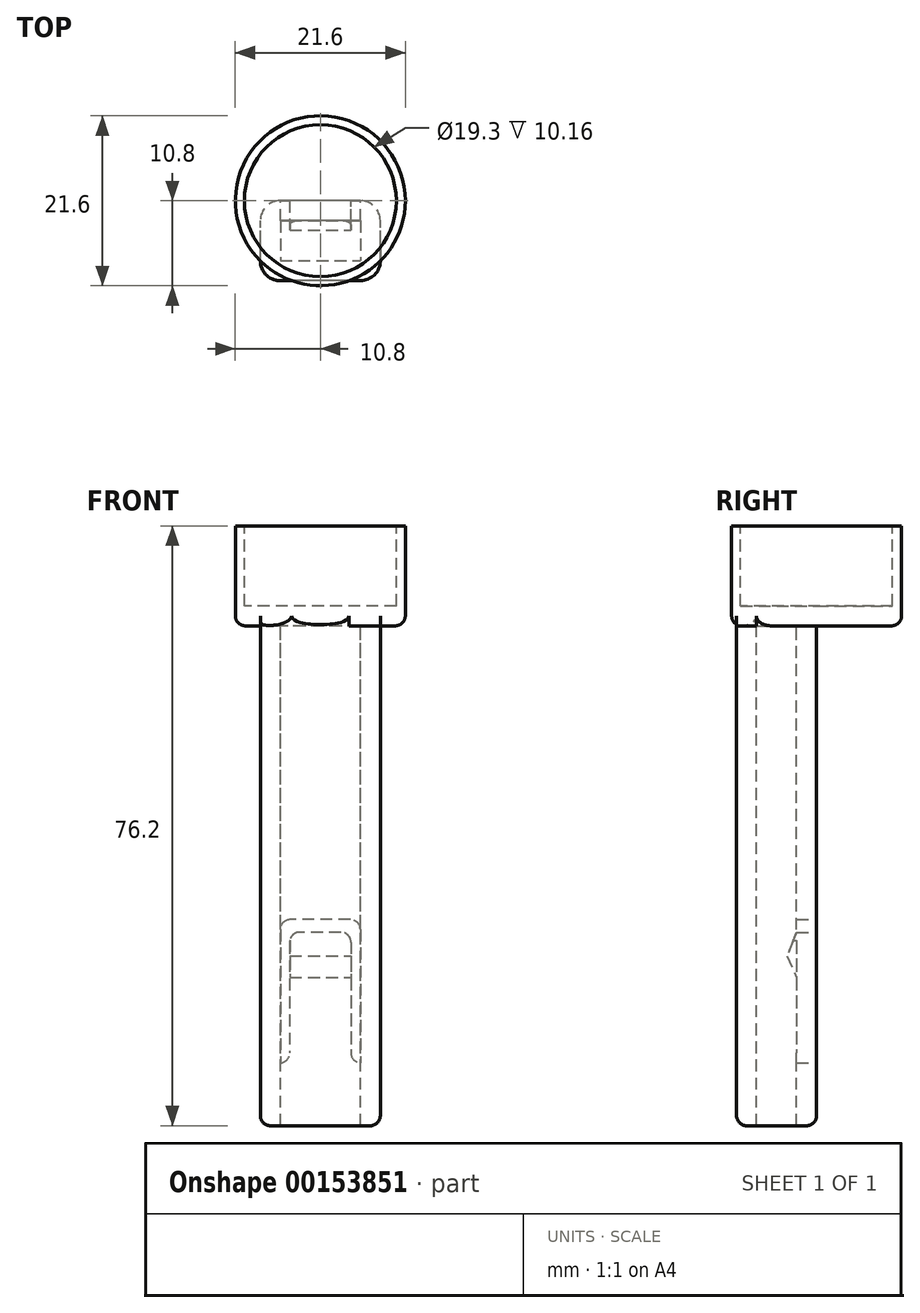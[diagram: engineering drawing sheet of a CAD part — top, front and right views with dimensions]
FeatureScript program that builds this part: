
annotation { "Feature Type Name" : "Feature", "Feature Type Description" : "" }
export const myFeature = defineFeature(function(context is Context, id is Id, definition is map)
    precondition{}
    {
        {
            var Q0;
            Q0=qCreatedBy(makeId("Top.planeOp"),FACE);
            var sketch = newSketch(context, id + "F0", { "sketchPlane" : qUnion([Q0])});
            skLineSegment(sketch, "E0.bottom", {"start": v(7.62, -5.08) * mm, "end": v(-7.62, -5.08) * mm});
            skLineSegment(sketch, "E0.top", {"start": v(7.62, 5.08) * mm, "end": v(-7.62, 5.08) * mm});
            skLineSegment(sketch, "E0.left", {"start": v(7.62, -5.08) * mm, "end": v(7.62, 5.08) * mm});
            skLineSegment(sketch, "E0.right", {"start": v(-7.62, -5.08) * mm, "end": v(-7.62, 5.08) * mm});
            skPoint(sketch, "E0.middle", {"position": v(0, 0) * mm});
            skSolve(sketch);
        }
        {
            var Q0;
            Q0 = qSketchRegion(id + "F0", true);
            extrude(context, id + "F1", {"entities" : qUnion([Q0]), "depth" : 63.5 * mm});
        }
        {
            var Q0;
            Q0=makeQuery(id+"F1.opExtrude","SWEPT_EDGE",EDGE,{"disambiguationData":[OSD([sQuery(id+"F0.wireOp",EDGE,"E0.bottom"),sQuery(id+"F0.wireOp",EDGE,"E0.left")])]});
            var Q1;
            Q1=makeQuery(id+"F1.opExtrude","SWEPT_EDGE",EDGE,{"disambiguationData":[OSD([sQuery(id+"F0.wireOp",EDGE,"E0.bottom"),sQuery(id+"F0.wireOp",EDGE,"E0.right")])]});
            var Q2;
            Q2=makeQuery(id+"F1.opExtrude","SWEPT_EDGE",EDGE,{"disambiguationData":[OSD([sQuery(id+"F0.wireOp",EDGE,"E0.top"),sQuery(id+"F0.wireOp",EDGE,"E0.left")])]});
            var Q3;
            Q3=makeQuery(id+"F1.opExtrude","SWEPT_EDGE",EDGE,{"disambiguationData":[OSD([sQuery(id+"F0.wireOp",EDGE,"E0.top"),sQuery(id+"F0.wireOp",EDGE,"E0.right")])]});
            fillet(context, id + "F2", {"entities" : qUnion([Q0, Q1, Q2, Q3]), "radius" : 2.54 * mm, "tangentPropagation" : true, "allowEdgeOverflow" : false});
        }
        {
            var Q0;
            Q0=makeQuery(id+"F1.opExtrude","CAP_FACE",FACE,{"disambiguationData":[OSD([sQuery(id+"F0.wireOp",EDGE,"E0.bottom"),sQuery(id+"F0.wireOp",EDGE,"E0.top"),sQuery(id+"F0.wireOp",EDGE,"E0.left"),sQuery(id+"F0.wireOp",EDGE,"E0.right")])],"isStart":false});
            shell(context, id + "F3", {"entities" : qUnion([Q0]), "thickness" : 2.54 * mm});
        }
        {
            var Q0;
            Q0=makeQuery(id+"F1.opExtrude","SWEPT_FACE",FACE,{"disambiguationData":[OSD([sQuery(id+"F0.wireOp",EDGE,"E0.top")])]});
            var sketch = newSketch(context, id + "F4", { "sketchPlane" : qUnion([Q0])});
            skLineSegment(sketch, "E1.bottom", {"start": v(-5.08, 26.19) * mm, "end": v(5.08, 26.19) * mm});
            skLineSegment(sketch, "E1.left", {"start": v(-5.08, 26.19) * mm, "end": v(-5.08, 6.36) * mm});
            skLineSegment(sketch, "E1.right", {"start": v(5.08, 26.19) * mm, "end": v(5.08, 6.36) * mm});
            skPoint(sketch, "E1.middle", {"position": v(0, 16.27) * mm});
            skLineSegment(sketch, "E2.bottom", {"start": v(-3.89, 24.58) * mm, "end": v(3.89, 24.58) * mm});
            skLineSegment(sketch, "E2.top", {"start": v(-3.89, 7.96) * mm, "end": v(3.89, 7.96) * mm});
            skLineSegment(sketch, "E2.left", {"start": v(-3.89, 24.58) * mm, "end": v(-3.89, 7.96) * mm});
            skLineSegment(sketch, "E2.right", {"start": v(3.89, 24.58) * mm, "end": v(3.89, 7.96) * mm});
            skLineSegment(sketch, "E3", {"start": v(5.08, 7.96) * mm, "end": v(-5.08, 7.96) * mm});
            skSolve(sketch);
        }
        {
            var Q0;
            {var subQ1=sQuery(id+"F4.wireOp",EDGE,"E1.bottom");Q0=makeQuery(id+"F4.imprint","IMPRINT",FACE,{"disambiguationData":[TD([[makeQuery(id+"F4.imprint","IMPRINT",EDGE,{"derivedFrom":subQ1}),-1.0]])]});}
            extrude(context, id + "F5", {"entities" : qUnion([Q0]), "operationType" : NewBodyOperationType.REMOVE, "endBound" : BoundingType.UP_TO_NEXT, "oppositeDirection" : true, "depth" : 25.4 * mm});
        }
        {
            var Q0;
            Q0=makeQuery(id+"F5.boolean.opBoolean","COPY",FACE,{"derivedFrom":makeQuery(id+"F5.opExtrude","SWEPT_FACE",FACE,{"disambiguationData":[OSD([sQuery(id+"F4.wireOp",EDGE,"E2.left")])]})});
            var sketch = newSketch(context, id + "F6", { "sketchPlane" : qUnion([Q0])});
            skLineSegment(sketch, "E4", {"start": v(2.54, 24.58) * mm, "end": v(1.34, 21.57) * mm});
            skLineSegment(sketch, "E5", {"start": v(1.34, 21.57) * mm, "end": v(2.54, 18.86) * mm});
            skLineSegment(sketch, "E6", {"start": v(2.54, 18.86) * mm, "end": v(2.54, 24.58) * mm});
            skSolve(sketch);
        }
        {
            var Q0;
            Q0 = qSketchRegion(id + "F6", true);
            extrude(context, id + "F7", {"entities" : qUnion([Q0]), "operationType" : NewBodyOperationType.ADD, "oppositeDirection" : true, "depth" : 7.75 * mm});
        }
        {
            var Q0;
            Q0=makeQuery(id+"F5.boolean.opBoolean","COPY",EDGE,{"derivedFrom":makeQuery(id+"F5.opExtrude","SWEPT_EDGE",EDGE,{"disambiguationData":[OSD([sQuery(id+"F4.wireOp",EDGE,"E2.bottom"),sQuery(id+"F4.wireOp",EDGE,"E2.right")])]})});
            var Q1;
            Q1=makeQuery(id+"F5.boolean.opBoolean","COPY",EDGE,{"derivedFrom":makeQuery(id+"F5.opExtrude","SWEPT_EDGE",EDGE,{"disambiguationData":[OSD([sQuery(id+"F4.wireOp",EDGE,"E2.bottom"),sQuery(id+"F4.wireOp",EDGE,"E2.left")])]})});
            var Q2;
            Q2=makeQuery(id+"F5.boolean.opBoolean","COPY",EDGE,{"derivedFrom":makeQuery(id+"F5.opExtrude","SWEPT_EDGE",EDGE,{"disambiguationData":[OSD([sQuery(id+"F4.wireOp",EDGE,"E2.right"),sQuery(id+"F4.wireOp",EDGE,"E3")])]})});
            var Q3;
            Q3=makeQuery(id+"F5.boolean.opBoolean","COPY",EDGE,{"derivedFrom":makeQuery(id+"F5.opExtrude","SWEPT_EDGE",EDGE,{"disambiguationData":[OSD([sQuery(id+"F4.wireOp",EDGE,"E2.left"),sQuery(id+"F4.wireOp",EDGE,"E3")])]})});
            var Q4;
            Q4=makeQuery(id+"F5.boolean.opBoolean","COPY",EDGE,{"derivedFrom":makeQuery(id+"F5.opExtrude","SWEPT_EDGE",EDGE,{"disambiguationData":[OSD([sQuery(id+"F0.wireOp",EDGE,"E0.top"),sQuery(id+"F0.wireOp",EDGE,"E0.left"),sQuery(id+"F4.wireOp",EDGE,"E1.bottom"),sQuery(id+"F4.wireOp",EDGE,"E1.left")])]})});
            var Q5;
            Q5=makeQuery(id+"F5.boolean.opBoolean","COPY",EDGE,{"derivedFrom":makeQuery(id+"F5.opExtrude","SWEPT_EDGE",EDGE,{"disambiguationData":[OSD([sQuery(id+"F0.wireOp",EDGE,"E0.top"),sQuery(id+"F0.wireOp",EDGE,"E0.right"),sQuery(id+"F4.wireOp",EDGE,"E1.bottom"),sQuery(id+"F4.wireOp",EDGE,"E1.right")])]})});
            fillet(context, id + "F8", {"entities" : qUnion([Q0, Q1, Q2, Q3, Q4, Q5]), "radius" : 1.27 * mm, "tangentPropagation" : true, "allowEdgeOverflow" : false});
        }
        {
            var Q0;
            Q0=makeQuery(id+"F3.opShell","OFFSET_FACE",FACE,{"disambiguationData":[OSD([sQuery(id+"F0.wireOp",EDGE,"E0.bottom"),sQuery(id+"F0.wireOp",EDGE,"E0.top"),sQuery(id+"F0.wireOp",EDGE,"E0.left"),sQuery(id+"F0.wireOp",EDGE,"E0.right")])]});
            extrude(context, id + "F9", {"entities" : qUnion([Q0]), "operationType" : NewBodyOperationType.REMOVE, "endBound" : BoundingType.UP_TO_NEXT, "oppositeDirection" : true, "depth" : 25.4 * mm});
        }
        {
            var Q0;
            Q0=makeQuery(id+"F1.opExtrude","CAP_EDGE",EDGE,{"disambiguationData":[OSD([sQuery(id+"F0.wireOp",EDGE,"E0.bottom")])],"isStart":true});
            var Q1;
            Q1=makeQuery(id+"F1.opExtrude","CAP_EDGE",EDGE,{"disambiguationData":[OSD([sQuery(id+"F0.wireOp",EDGE,"E0.top")])],"isStart":true});
            var Q2;
            {var subQ0=sQuery(id+"F0.wireOp",EDGE,"E0.right");var subQ1=sQuery(id+"F0.wireOp",EDGE,"E0.top");Q2=makeQuery(id+"F2.opFillet","BLEND_EDGE",EDGE,{"blendedFrom":[makeQuery(id+"F1.opExtrude","SWEPT_EDGE",EDGE,{"disambiguationData":[OSD([subQ1,subQ0])]}),makeQuery(id+"F1.opExtrude","CAP_FACE",FACE,{"disambiguationData":[OSD([sQuery(id+"F0.wireOp",EDGE,"E0.bottom"),subQ1,sQuery(id+"F0.wireOp",EDGE,"E0.left"),subQ0])],"isStart":true})],"blendedInto":[makeQuery(id+"F1.opExtrude","CAP_FACE",FACE,{"disambiguationData":[OSD([sQuery(id+"F0.wireOp",EDGE,"E0.bottom"),subQ1,sQuery(id+"F0.wireOp",EDGE,"E0.left"),subQ0])],"isStart":true})]});}
            var Q3;
            Q3=makeQuery(id+"F1.opExtrude","CAP_EDGE",EDGE,{"disambiguationData":[OSD([sQuery(id+"F0.wireOp",EDGE,"E0.right")])],"isStart":true});
            var Q4;
            {var subQ0=sQuery(id+"F0.wireOp",EDGE,"E0.right");var subQ1=sQuery(id+"F0.wireOp",EDGE,"E0.bottom");Q4=makeQuery(id+"F2.opFillet","BLEND_EDGE",EDGE,{"blendedFrom":[makeQuery(id+"F1.opExtrude","SWEPT_EDGE",EDGE,{"disambiguationData":[OSD([subQ1,subQ0])]}),makeQuery(id+"F1.opExtrude","CAP_FACE",FACE,{"disambiguationData":[OSD([subQ1,sQuery(id+"F0.wireOp",EDGE,"E0.top"),sQuery(id+"F0.wireOp",EDGE,"E0.left"),subQ0])],"isStart":true})],"blendedInto":[makeQuery(id+"F1.opExtrude","CAP_FACE",FACE,{"disambiguationData":[OSD([subQ1,sQuery(id+"F0.wireOp",EDGE,"E0.top"),sQuery(id+"F0.wireOp",EDGE,"E0.left"),subQ0])],"isStart":true})]});}
            var Q5;
            {var subQ0=sQuery(id+"F0.wireOp",EDGE,"E0.left");var subQ1=sQuery(id+"F0.wireOp",EDGE,"E0.top");Q5=makeQuery(id+"F2.opFillet","BLEND_EDGE",EDGE,{"blendedFrom":[makeQuery(id+"F1.opExtrude","SWEPT_EDGE",EDGE,{"disambiguationData":[OSD([subQ1,subQ0])]}),makeQuery(id+"F1.opExtrude","CAP_FACE",FACE,{"disambiguationData":[OSD([sQuery(id+"F0.wireOp",EDGE,"E0.bottom"),subQ1,subQ0,sQuery(id+"F0.wireOp",EDGE,"E0.right")])],"isStart":true})],"blendedInto":[makeQuery(id+"F1.opExtrude","CAP_FACE",FACE,{"disambiguationData":[OSD([sQuery(id+"F0.wireOp",EDGE,"E0.bottom"),subQ1,subQ0,sQuery(id+"F0.wireOp",EDGE,"E0.right")])],"isStart":true})]});}
            var Q6;
            {var subQ0=sQuery(id+"F0.wireOp",EDGE,"E0.left");var subQ1=sQuery(id+"F0.wireOp",EDGE,"E0.bottom");Q6=makeQuery(id+"F2.opFillet","BLEND_EDGE",EDGE,{"blendedFrom":[makeQuery(id+"F1.opExtrude","SWEPT_EDGE",EDGE,{"disambiguationData":[OSD([subQ1,subQ0])]}),makeQuery(id+"F1.opExtrude","CAP_FACE",FACE,{"disambiguationData":[OSD([subQ1,sQuery(id+"F0.wireOp",EDGE,"E0.top"),subQ0,sQuery(id+"F0.wireOp",EDGE,"E0.right")])],"isStart":true})],"blendedInto":[makeQuery(id+"F1.opExtrude","CAP_FACE",FACE,{"disambiguationData":[OSD([subQ1,sQuery(id+"F0.wireOp",EDGE,"E0.top"),subQ0,sQuery(id+"F0.wireOp",EDGE,"E0.right")])],"isStart":true})]});}
            var Q7;
            Q7=makeQuery(id+"F1.opExtrude","CAP_EDGE",EDGE,{"disambiguationData":[OSD([sQuery(id+"F0.wireOp",EDGE,"E0.left")])],"isStart":true});
            fillet(context, id + "F10", {"entities" : qUnion([Q0, Q1, Q2, Q3, Q4, Q5, Q6, Q7]), "radius" : 1.27 * mm, "tangentPropagation" : true, "allowEdgeOverflow" : false});
        }
        {
            var Q0;
            Q0=makeQuery(id+"F1.opExtrude","CAP_FACE",FACE,{"disambiguationData":[OSD([sQuery(id+"F0.wireOp",EDGE,"E0.bottom"),sQuery(id+"F0.wireOp",EDGE,"E0.top"),sQuery(id+"F0.wireOp",EDGE,"E0.left"),sQuery(id+"F0.wireOp",EDGE,"E0.right")])],"isStart":false});
            var sketch = newSketch(context, id + "F11", { "sketchPlane" : qUnion([Q0])});
            skCircle(sketch, "E7", {"center": v(0, 5.08) * mm, "radius": 10.8 * mm});
            skSolve(sketch);
        }
        {
            var Q0;
            Q0 = qSketchRegion(id + "F11", true);
            extrude(context, id + "F12", {"entities" : qUnion([Q0]), "operationType" : NewBodyOperationType.ADD, "depth" : 12.7 * mm});
        }
        {
            var Q0;
            {var subQ0=sQuery(id+"F0.wireOp",EDGE,"E0.left");var subQ1=sQuery(id+"F0.wireOp",EDGE,"E0.bottom");var subQ2=sQuery(id+"F11.wireOp",EDGE,"E7");var subQ3=makeQuery(id+"F12.opExtrude","SWEPT_FACE",FACE,{"disambiguationData":[OSD([subQ2])]});var subQ5=makeQuery(id+"F12.opExtrude","CAP_FACE",FACE,{"disambiguationData":[OSD([subQ2])],"isStart":true});Q0=makeQuery(id+"F12.boolean.opBoolean","SPLIT",EDGE,{"disambiguationData":[topologyDisambiguationEdgeConnected([subQ3,subQ5]),TD([makeQuery(id+"F2.opFillet","BLEND_FACE",FACE,{"disambiguationData":[OSD([subQ1,subQ0])]})])],"derivedFrom":makeQuery(id+"F12.opExtrude","CAP_EDGE",EDGE,{"disambiguationData":[OSD([subQ2])],"isStart":true})});}
            var Q1;
            {var subQ0=sQuery(id+"F0.wireOp",EDGE,"E0.bottom");var subQ1=sQuery(id+"F11.wireOp",EDGE,"E7");var subQ2=makeQuery(id+"F12.opExtrude","SWEPT_FACE",FACE,{"disambiguationData":[OSD([subQ1])]});var subQ3=makeQuery(id+"F12.opExtrude","CAP_FACE",FACE,{"disambiguationData":[OSD([subQ1])],"isStart":true});Q1=makeQuery(id+"F12.boolean.opBoolean","SPLIT",EDGE,{"disambiguationData":[topologyDisambiguationEdgeConnected([subQ2,subQ3]),TD([makeQuery(id+"F1.opExtrude","SWEPT_FACE",FACE,{"disambiguationData":[OSD([subQ0])]})])],"derivedFrom":makeQuery(id+"F12.opExtrude","CAP_EDGE",EDGE,{"disambiguationData":[OSD([subQ1])],"isStart":true})});}
            fillet(context, id + "F13", {"entities" : qUnion([Q0, Q1]), "radius" : 1.27 * mm, "tangentPropagation" : true, "allowEdgeOverflow" : false});
        }
        {
            var Q0;
            {var subQ0=sQuery(id+"F0.wireOp",EDGE,"E0.left");var subQ1=sQuery(id+"F0.wireOp",EDGE,"E0.bottom");var subQ2=sQuery(id+"F11.wireOp",EDGE,"E7");var subQ3=makeQuery(id+"F12.opExtrude","SWEPT_FACE",FACE,{"disambiguationData":[OSD([subQ2])]});var subQ4=makeQuery(id+"F1.opExtrude","CAP_FACE",FACE,{"disambiguationData":[OSD([subQ1,sQuery(id+"F0.wireOp",EDGE,"E0.top"),subQ0,sQuery(id+"F0.wireOp",EDGE,"E0.right")])],"isStart":false});Q0=makeQuery(id+"F12.boolean.opBoolean","SPLIT",EDGE,{"disambiguationData":[topologyDisambiguationEdgeConnected([subQ4,subQ3]),TD([makeQuery(id+"F2.opFillet","BLEND_FACE",FACE,{"disambiguationData":[OSD([subQ1,subQ0])]})])],"derivedFrom":makeQuery(id+"F12.opExtrude","CAP_EDGE",EDGE,{"disambiguationData":[OSD([subQ2])],"isStart":true})});}
            var Q1;
            {var subQ0=sQuery(id+"F11.wireOp",EDGE,"E7");var subQ1=makeQuery(id+"F12.opExtrude","SWEPT_FACE",FACE,{"disambiguationData":[OSD([subQ0])]});var subQ2=sQuery(id+"F0.wireOp",EDGE,"E0.right");var subQ3=sQuery(id+"F0.wireOp",EDGE,"E0.bottom");var subQ4=makeQuery(id+"F1.opExtrude","CAP_FACE",FACE,{"disambiguationData":[OSD([subQ3,sQuery(id+"F0.wireOp",EDGE,"E0.top"),sQuery(id+"F0.wireOp",EDGE,"E0.left"),subQ2])],"isStart":false});Q1=makeQuery(id+"F12.boolean.opBoolean","SPLIT",EDGE,{"disambiguationData":[topologyDisambiguationEdgeConnected([subQ4,subQ1]),TD([makeQuery(id+"F2.opFillet","BLEND_FACE",FACE,{"disambiguationData":[OSD([subQ3,subQ2])]})])],"derivedFrom":makeQuery(id+"F12.opExtrude","CAP_EDGE",EDGE,{"disambiguationData":[OSD([subQ0])],"isStart":true})});}
            fillet(context, id + "F14", {"entities" : qUnion([Q0, Q1]), "radius" : 1.27 * mm, "tangentPropagation" : true, "allowEdgeOverflow" : false});
        }
        {
            var Q0;
            Q0=makeQuery(id+"F12.opExtrude","CAP_FACE",FACE,{"disambiguationData":[OSD([sQuery(id+"F11.wireOp",EDGE,"E7")])],"isStart":false});
            var sketch = newSketch(context, id + "F15", { "sketchPlane" : qUnion([Q0])});
            skCircle(sketch, "E8", {"center": v(0, 5.08) * mm, "radius": 9.65 * mm});
            skSolve(sketch);
        }
        {
            var Q0;
            Q0 = qSketchRegion(id + "F15", true);
            extrude(context, id + "F16", {"entities" : qUnion([Q0]), "operationType" : NewBodyOperationType.REMOVE, "oppositeDirection" : true, "depth" : 10.16 * mm});
        }
    });
